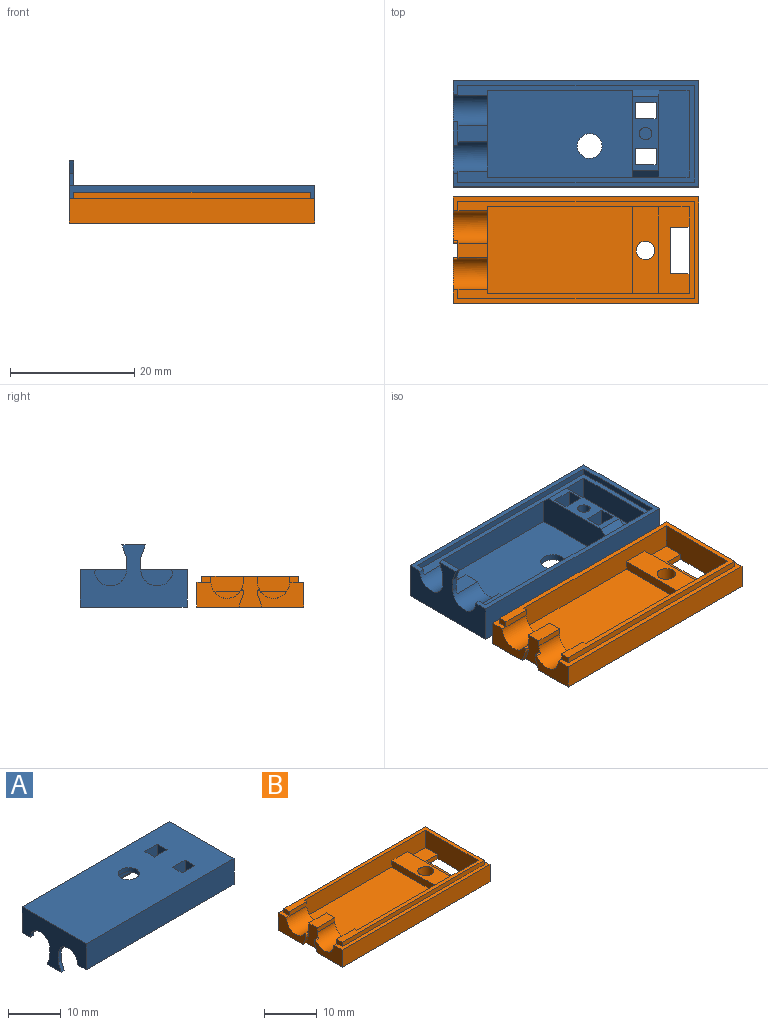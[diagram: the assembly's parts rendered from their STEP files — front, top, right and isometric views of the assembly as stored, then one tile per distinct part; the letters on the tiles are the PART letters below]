
ASSEMBLY  parts=2 mates=2
PART A: 45 faces, bbox 39.6x17.2x10 mm
  f0: plane 39.6x17.2mm, normal (0,0,1), area 651mm2, adj f8,f19,f20,f21,f25,f26,f27,f28
  f1: plane 4.9x4mm, normal (0,-1,0), area 19.6mm2, adj f4,f11,f14,f24
  f2: plane 4.9x4mm, normal (0,1,0), area 19.6mm2, adj f4,f11,f14,f24
  f3: plane 23.4x14mm, normal (0,0,-1), area 315mm2, adj f9,f10,f12,f31,f37
  f4: plane 38x15.6mm, normal (0,0,-1), area 80mm2, adj f1,f2,f5,f9,f10,f11,f12,f15
  f5: plane 1.65x1mm, normal (1,0,0), area 1.5mm2, adj f4,f7,f17,f23
  f6: plane 5x3.76mm, normal (1,0,0), area 13.1mm2, adj f13,f22,f23,f40,f41,f42,f43,f44
  f7: plane 39.6x17.2mm, normal (0,0,-1), area 78.2mm2, adj f5,f8,f15,f16,f17,f18,f19,f20
  f8: plane 17.2x10mm, normal (-1,0,0), area 92.6mm2, adj f0,f7,f19,f21,f22,f23,f40,f41
  f9: plane 14x4mm, normal (1,0,0), area 44.9mm2, adj f3,f4,f10,f12,f13,f22,f23
  f10: plane 23.4x4mm, normal (0,-1,0), area 93.6mm2, adj f3,f4,f9,f31
  f11: plane 14x4mm, normal (-1,0,0), area 56mm2, adj f1,f2,f4,f14
  f12: plane 23.4x4mm, normal (0,1,0), area 93.6mm2, adj f3,f4,f9,f31
  f13: plane 4.7x2.7mm, normal (0,0,-1), area 12.7mm2, adj f6,f9,f22,f23
  f14: plane 14x4.9mm, normal (0,0,-1), area 68.6mm2, adj f1,f2,f11,f24
  f15: plane 38x1mm, normal (0,1,0), area 38mm2, adj f4,f7,f16,f18
  f16: plane 1.65x1mm, normal (1,0,0), area 1.5mm2, adj f4,f7,f15,f22
  f17: plane 38x1mm, normal (0,-1,0), area 38mm2, adj f4,f5,f7,f18
  f18: plane 15.6x1mm, normal (-1,0,0), area 15.6mm2, adj f4,f7,f15,f17
  f19: plane 39.6x6mm, normal (0,-1,0), area 237.6mm2, adj f0,f7,f8,f20
  f20: plane 17.2x6mm, normal (1,0,0), area 103.2mm2, adj f0,f7,f19,f21
  f21: plane 39.6x6mm, normal (0,1,0), area 237.6mm2, adj f0,f7,f8,f20
  f22: cylinder r=2.6mm len=5.5mm, axis (-1,0,0), area 35.3mm2, adj f4,f6,f7,f8,f9,f13,f16,f44
  f23: cylinder r=2.6mm len=5.5mm, axis (-1,0,0), area 35.3mm2, adj f4,f5,f6,f7,f8,f9,f13,f40
  f24: plane 14x5mm, normal (1,0,0), area 69mm2, adj f1,f2,f14,f35,f38,f39
  f25: plane 6x2.6mm, normal (-1,0,0), area 15.6mm2, adj f0,f26,f32,f35
  f26: plane 6x3.38mm, normal (0,1,0), area 20.3mm2, adj f0,f25,f27,f35
  f27: plane 6x2.6mm, normal (1,0,0), area 15.6mm2, adj f0,f26,f32,f35
  f28: plane 6x2.6mm, normal (-1,0,0), area 15.6mm2, adj f0,f29,f33,f35
  f29: plane 6x3.38mm, normal (0,1,0), area 20.3mm2, adj f0,f28,f30,f35
  f30: plane 6x2.6mm, normal (1,0,0), area 15.6mm2, adj f0,f29,f33,f35
  f31: plane 14x5mm, normal (-1,0,0), area 69mm2, adj f3,f10,f12,f35,f38,f39
  f32: plane 6x3.38mm, normal (0,-1,0), area 20.3mm2, adj f0,f25,f27,f35
  f33: plane 6x3.38mm, normal (0,-1,0), area 20.3mm2, adj f0,f28,f30,f35
  f34: cylinder r=1mm len=5mm, axis (0,0,1), area 31.4mm2, adj f35,f36
  f35: plane 12x4.2mm, normal (0,0,-1), area 29.7mm2, adj f24,f25,f26,f27,f28,f29,f30,f31
  f36: plane 2x2mm, normal (0,0,-1), area 3.1mm2, adj f34
  f37: cylinder r=2mm len=4mm, axis (0,0,1), area 12.6mm2, adj f0,f3
  f38: plane 4.2x1mm, normal (0,0.71,-0.71), area 5.9mm2, adj f4,f24,f31,f35
  f39: plane 4.2x1mm, normal (0,-0.71,-0.71), area 5.9mm2, adj f4,f24,f31,f35
  f40: plane 2x0.8mm, normal (0,1,0), area 1.6mm2, adj f6,f8,f23,f41
  f41: plane 2x0.8mm, normal (0,0.94,0.34), area 1.7mm2, adj f6,f8,f40,f42
  f42: plane 3.76x0.8mm, normal (0,0,-1), area 3mm2, adj f6,f8,f41,f43
  f43: plane 2x0.8mm, normal (0,-0.94,0.34), area 1.7mm2, adj f6,f8,f42,f44
  f44: plane 2x0.8mm, normal (0,-1,0), area 1.6mm2, adj f6,f8,f22,f43
PART B: 40 faces, bbox 39.6x17.2x5 mm
  f0: plane 7.45x4mm, normal (-1,0,0), area 18.3mm2, adj f4,f11,f12,f22,f34,f35,f38
  f1: plane 23.4x14mm, normal (0,0,1), area 327.6mm2, adj f2,f8,f15,f32
  f2: plane 32.5x4mm, normal (0,-1,0), area 123.7mm2, adj f1,f3,f5,f8,f14,f31,f32,f33
  f3: plane 14x4.9mm, normal (0,0,1), area 46.1mm2, adj f2,f14,f15,f28,f29,f30,f31
  f4: plane 39.6x17.2mm, normal (0,0,-1), area 648.5mm2, adj f0,f7,f13,f14,f20,f21,f22,f27
  f5: plane 38x15.6mm, normal (0,0,1), area 78.1mm2, adj f2,f6,f8,f14,f15,f16,f17,f18
  f6: plane 1.45x1mm, normal (-1,0,0), area 1.4mm2, adj f5,f12,f18,f26
  f7: plane 5x3.76mm, normal (-1,0,0), area 13.2mm2, adj f4,f9,f10,f11,f24,f25,f34,f35
  f8: plane 14x4mm, normal (1,0,0), area 24.4mm2, adj f1,f2,f5,f9,f10,f11,f15,f23
  f9: plane 4.7x2.3mm, normal (0,0,1), area 10.8mm2, adj f7,f8,f24,f25
  f10: cylinder r=2.6mm len=5.5mm, axis (-1,0,0), area 43.8mm2, adj f7,f8,f12,f13,f23,f24,f39
  f11: cylinder r=2.6mm len=5.5mm, axis (-1,0,0), area 43.8mm2, adj f0,f7,f8,f12,f25,f26,f38
  f12: plane 39.6x17.2mm, normal (0,0,1), area 78.2mm2, adj f0,f6,f10,f11,f13,f16,f17,f18
  f13: plane 7.45x4mm, normal (-1,0,0), area 18.3mm2, adj f4,f10,f12,f21,f36,f37,f39
  f14: plane 14x5mm, normal (-1,0,0), area 63.5mm2, adj f2,f3,f4,f5,f15,f28,f30
  f15: plane 32.5x4mm, normal (0,1,0), area 123.7mm2, adj f1,f3,f5,f8,f14,f31,f32,f33
  f16: plane 38x1mm, normal (0,-1,0), area 38mm2, adj f5,f12,f17,f19
  f17: plane 1.45x1mm, normal (-1,0,0), area 1.4mm2, adj f5,f12,f16,f23
  f18: plane 38x1mm, normal (0,1,0), area 38mm2, adj f5,f6,f12,f19
  f19: plane 15.6x1mm, normal (1,0,0), area 15.6mm2, adj f5,f12,f16,f18
  f20: plane 17.2x4mm, normal (1,0,0), area 68.8mm2, adj f4,f12,f21,f22
  f21: plane 39.6x4mm, normal (0,-1,0), area 158.4mm2, adj f4,f12,f13,f20
  f22: plane 39.6x4mm, normal (0,1,0), area 158.4mm2, adj f0,f4,f12,f20
  f23: plane 4.7x1mm, normal (0,1,0), area 4.7mm2, adj f5,f8,f10,f17
  f24: plane 4.7x1mm, normal (0,-1,0), area 4.7mm2, adj f7,f8,f9,f10
  f25: plane 4.7x1mm, normal (0,1,0), area 4.7mm2, adj f7,f8,f9,f11
  f26: plane 4.7x1mm, normal (0,-1,0), area 4.7mm2, adj f5,f6,f8,f11
  f27: cylinder r=1.5mm len=3mm, axis (0,0,1), area 23.6mm2, adj f4,f33
  f28: plane 3x1mm, normal (0,-1,0), area 3mm2, adj f3,f4,f14,f29
  f29: plane 7.5x1mm, normal (1,0,0), area 7.5mm2, adj f3,f4,f28,f30
  f30: plane 3x1mm, normal (0,1,0), area 3mm2, adj f3,f4,f14,f29
  f31: plane 14x1.5mm, normal (1,0,0), area 21mm2, adj f2,f3,f15,f33
  f32: plane 14x1.5mm, normal (-1,0,0), area 21mm2, adj f1,f2,f15,f33
  f33: plane 14x4.2mm, normal (0,0,1), area 51.7mm2, adj f2,f15,f27,f31,f32
  f34: plane 0.8x0.56mm, normal (0,-1,0), area 0.4mm2, adj f0,f7,f35,f38
  f35: plane 2x0.8mm, normal (0,-0.94,-0.34), area 1.7mm2, adj f0,f4,f7,f34
  f36: plane 2x0.8mm, normal (0,0.94,-0.34), area 1.7mm2, adj f4,f7,f13,f37
  f37: plane 0.8x0.56mm, normal (0,1,0), area 0.4mm2, adj f7,f13,f36,f39
  f38: cylinder r=0.2mm len=0.8mm, axis (-1,0,0), area 0.4mm2, adj f0,f7,f11,f34
  f39: cylinder r=0.2mm len=0.8mm, axis (-1,0,0), area 0.4mm2, adj f7,f10,f13,f37
PLACE A rot(axis=(1,0,0),180deg) t=(0,18.8,10)mm
PLACE B at identity fixed
MATE planar B.f4 <-> A.f0  axis (0,0,-1) through (-2.81,0,0)mm
MATE planar A.f20 <-> B.f20  axis (1,0,0) through (17.6,18.8,3)mm
